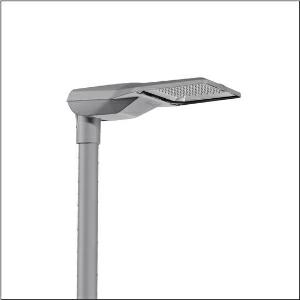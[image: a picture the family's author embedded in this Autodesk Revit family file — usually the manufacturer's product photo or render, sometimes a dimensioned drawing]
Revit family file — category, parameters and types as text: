
# Revit family: streetlight_sl_21_midi___stw1_0a_5xe7e33a08nb_8300
name_source: partatom
category: Lighting Fixtures
units: mm (PartAtom-declared; Revit-internal decimal feet)

## family parameters
Cut with Voids When Loaded = No
Host = Face
Light Source = No
Part Type = Normal
Room Calculation Point = No
Round Connector Dimension = Use Diameter
Shared = No

## types (1)
- --- (1 x LED, 22700 lm, 151.2 W, 3000K)
    Apparent Load = 151 VA
    CIE Flux Codes = 39 75 98 100 100
    Color Rendering = 70
    Color Temperature = 3000K
    Default Elevation = 1800 mm
    Description = Streetlight SL 21 midi, mast luminaire, primary light control with lens, of PMMA, primary optical cover: cover, of toughened safety glass, transparent, light distribution: STW1.0a, light emission: direct distribution, primary light characteristic: asymmetric, installation type: post-top, side-entry, LED, 3G 1.5mm², High Power LED, rated luminous flux: 22.700lm, luminous efficacy: 150lm/W, light colour: 730, colour temperature: 3000K, control: overheat protection, constant luminous flux control, time-dependent luminous flux control, flexible luminous flux parameterisation, mains connection: 220..240V, AC, 50/60Hz, connection cable pre-assembled, cable length: 12,5m, wiring characteristics: H07RN-F, start of lifetime: 151W, end of service life: 157W, reduction: 70W, luminaire housing, of diecast aluminium, powder-coated, Siteco® metallic grey (DB 702S), corrosivity category C5 mid according to DIN EN ISO 12944, please order mast flange separately, inclination adjustable: 0°, 5°, 10°, 15°, sealing non-destructively replaceable, multi-level sealing system, length: 644mm, width: 335mm, height: 110mm, mast flange for spigot size: 42mm (side-entry): 5XC10008XM4, 60/48mm (side-entry/post-top): 5XC10108XM2, 76/60mm (side-entry/post-top): 5XC10108XM1, protection rating (complete): IP66, insulation class (complete): insulation class II (safety insulation), certification: CE, ENEC, ENEC+, VDE, impact resistance: IK09, permissible operating ambient temperature for outdoor applications: -40..+50°C, standard-compliant lighting for roads and squares, packaging unit: 1 piece

Light Distribution: STW1.0a
    Height = 111 mm
    Lamp = 1 x LED
    Lamp Light Flux = 22700 lm
    Lamp Power = 151.2 W
    Lamp count = 1
    Length = 644 mm
    Luminous efficacy = 150 lm/W
    Manufacturer = Siteco
    ModVariant = No
    Model = 5XE7E33A08NB
    Number of Poles = 1
    OnlyDefault = Yes
    Power Factor = 1
    Product Name = Streetlight SL 21 midi | STW1.0a
    Product group = mast luminaire | pylon top
    ProductGroupID = 6100
    Protection Class = Protection class II
    Protection Degree = IP 66
    RLX_Detail_Level = 1
    RLX_Emergency_Light_Flux = 0 lm
    RLX_Emergency_Type = 0
    RLX_Emergency_Type_DB = No
    RlxData = <blob elided: 90877 chars, md5=a86e6c22>
    Socket = socket
    Standby Power = 0 W
    System Light Flux = 22700 lm
    System Power = 151 W
    Type Comments = factory setting: luminous flux: 100 % | Output Level: 100 % | 802 mA
    Type Image = l_1004298.jpg
    URL = http://relux.com
    VarID = @adj_140035
    Voltage = 0 V
    Weight = 0.00 kg
    Width = 336 mm

## geometry (parser evidence)
native form markers: Blend x4, Sweep x10
no freeform markers — native parametric forms only
